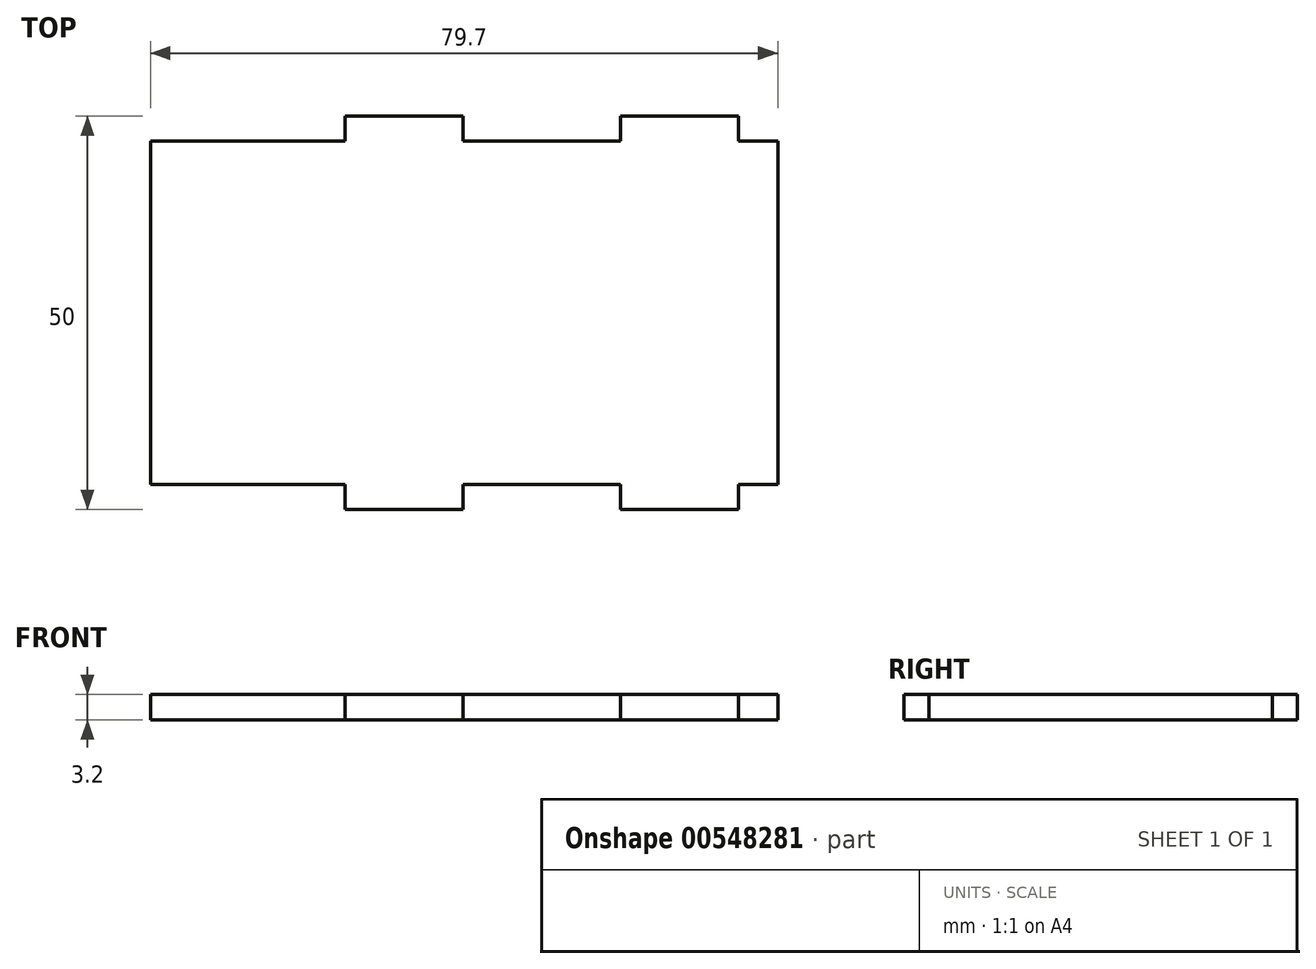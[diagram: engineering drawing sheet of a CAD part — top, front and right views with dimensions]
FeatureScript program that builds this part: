
annotation { "Feature Type Name" : "Feature", "Feature Type Description" : "" }
export const myFeature = defineFeature(function(context is Context, id is Id, definition is map)
    precondition{}
    {
        {
            var Q0;
            Q0=qCreatedBy(makeId("Top.planeOp"),FACE);
            var sketch = newSketch(context, id + "F0", { "sketchPlane" : qUnion([Q0])});
            skLineSegment(sketch, "E0.bottom", {"start": v(33.25, 0) * mm, "end": v(-46.45, 0) * mm});
            skLineSegment(sketch, "E0.top", {"start": v(33.25, 43.6) * mm, "end": v(-46.45, 43.6) * mm});
            skLineSegment(sketch, "E0.left", {"start": v(33.25, 0) * mm, "end": v(33.25, 43.6) * mm});
            skLineSegment(sketch, "E0.right", {"start": v(-46.45, 0) * mm, "end": v(-46.45, 43.6) * mm});
            skLineSegment(sketch, "E1.bottom", {"start": v(-21.75, 43.6) * mm, "end": v(-6.75, 43.6) * mm});
            skLineSegment(sketch, "E1.top", {"start": v(-21.75, 46.8) * mm, "end": v(-6.75, 46.8) * mm});
            skLineSegment(sketch, "E1.left", {"start": v(-21.75, 43.6) * mm, "end": v(-21.75, 46.8) * mm});
            skLineSegment(sketch, "E1.right", {"start": v(-6.75, 43.6) * mm, "end": v(-6.75, 46.8) * mm});
            skLineSegment(sketch, "E2.bottom", {"start": v(13.25, 43.6) * mm, "end": v(28.25, 43.6) * mm});
            skLineSegment(sketch, "E2.top", {"start": v(13.25, 46.8) * mm, "end": v(28.25, 46.8) * mm});
            skLineSegment(sketch, "E2.left", {"start": v(13.25, 43.6) * mm, "end": v(13.25, 46.8) * mm});
            skLineSegment(sketch, "E2.right", {"start": v(28.25, 43.6) * mm, "end": v(28.25, 46.8) * mm});
            skLineSegment(sketch, "E3.bottom", {"start": v(-21.75, 0) * mm, "end": v(-6.75, 0) * mm});
            skLineSegment(sketch, "E3.top", {"start": v(-21.75, -3.2) * mm, "end": v(-6.75, -3.2) * mm});
            skLineSegment(sketch, "E3.left", {"start": v(-21.75, 0) * mm, "end": v(-21.75, -3.2) * mm});
            skLineSegment(sketch, "E3.right", {"start": v(-6.75, 0) * mm, "end": v(-6.75, -3.2) * mm});
            skLineSegment(sketch, "E4.bottom", {"start": v(13.25, 0) * mm, "end": v(28.25, 0) * mm});
            skLineSegment(sketch, "E4.top", {"start": v(13.25, -3.2) * mm, "end": v(28.25, -3.2) * mm});
            skLineSegment(sketch, "E4.left", {"start": v(13.25, 0) * mm, "end": v(13.25, -3.2) * mm});
            skLineSegment(sketch, "E4.right", {"start": v(28.25, 0) * mm, "end": v(28.25, -3.2) * mm});
            skSolve(sketch);
        }
        {
            var Q0;
            Q0=qSketchRegion(id+"F0",true);
            extrude(context, id + "F1", {"entities" : qUnion([Q0]), "depth" : 3.2 * mm, "offsetDistance" : 25 * mm});
        }
    });
